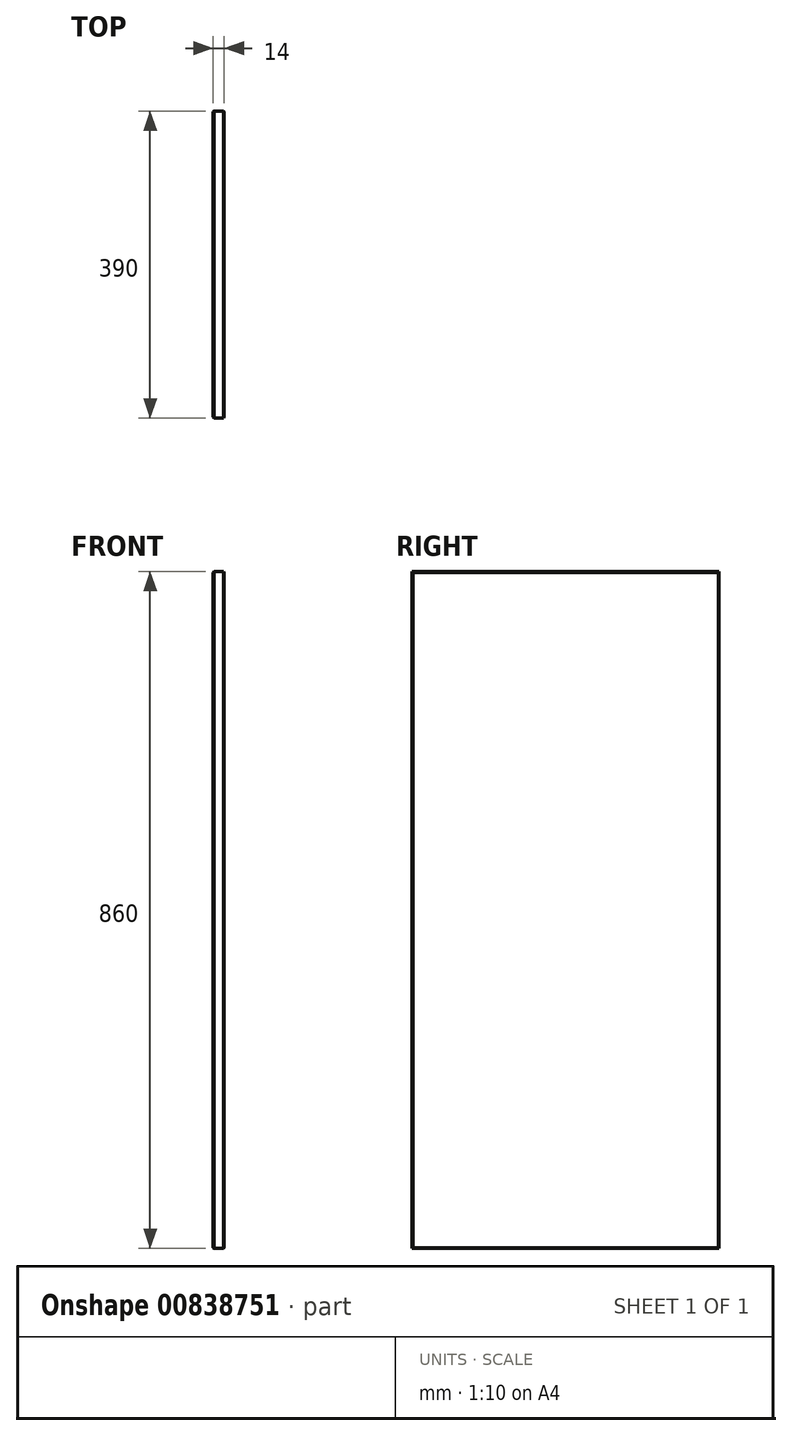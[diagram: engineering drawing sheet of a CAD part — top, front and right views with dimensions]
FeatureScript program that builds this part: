
annotation { "Feature Type Name" : "Feature", "Feature Type Description" : "" }
export const myFeature = defineFeature(function(context is Context, id is Id, definition is map)
    precondition{}
    {
        {
            var Q0;
            Q0=qCreatedBy(makeId("Right.planeOp"),FACE);
            var sketch = newSketch(context, id + "F0", { "sketchPlane" : qUnion([Q0])});
            skLineSegment(sketch, "E0.bottom", {"start": v(0, 0) * mm, "end": v(-55.42, 0) * mm});
            skLineSegment(sketch, "E0.top", {"start": v(0, 42.97) * mm, "end": v(-55.42, 42.97) * mm});
            skLineSegment(sketch, "E0.left", {"start": v(0, 0) * mm, "end": v(0, 42.97) * mm});
            skLineSegment(sketch, "E0.right", {"start": v(-55.42, 0) * mm, "end": v(-55.42, 42.97) * mm});
            skSolve(sketch);
        }
        {
            var Q0;
            Q0=makeQuery(id+"F0.imprint","IMPRINT",FACE,{"disambiguationData":[TD([[makeQuery(id+"F0.imprint","IMPRINT",EDGE,{"derivedFrom":sQuery(id+"F0.wireOp",EDGE,"E0.bottom")}),-1.0]])]});
            extrude(context, id + "F1", {"entities" : qUnion([Q0]), "oppositeDirection" : true, "depth" : 14 * mm, "offsetDistance" : 25 * mm});
        }
        {
            var Q0;
            Q0=makeQuery(id+"F1.opExtrude","SWEPT_FACE",FACE,{"disambiguationData":[OSD([sQuery(id+"F0.wireOp",EDGE,"E0.bottom")])]});
            extrude(context, id + "F2", {"entities" : qUnion([Q0]), "operationType" : NewBodyOperationType.ADD, "oppositeDirection" : true, "depth" : 1060 * mm, "offsetDistance" : 25 * mm});
        }
        {
            var Q0;
            {var subQ0=sQuery(id+"F0.wireOp",EDGE,"E0.left");Q0=makeQuery(id+"F2.boolean.opBoolean","MERGE",FACE,{"derivedFrom":[makeQuery(id+"F1.opExtrude","SWEPT_FACE",FACE,{"disambiguationData":[OSD([subQ0])]}),makeQuery(id+"F2.opExtrude","SWEPT_FACE",FACE,{"disambiguationData":[OSD([sQuery(id+"F0.wireOp",EDGE,"E0.bottom"),subQ0])]})]});}
            extrude(context, id + "F3", {"entities" : qUnion([Q0]), "operationType" : NewBodyOperationType.ADD, "oppositeDirection" : true, "depth" : 390 * mm, "offsetDistance" : 25 * mm});
        }
        {
            var Q0;
            {var subQ0=sQuery(id+"F0.wireOp",EDGE,"E0.left");var subQ1=sQuery(id+"F0.wireOp",EDGE,"E0.bottom");Q0=makeQuery(id+"F3.boolean.opBoolean","MERGE",FACE,{"derivedFrom":[makeQuery(id+"F2.opExtrude","CAP_FACE",FACE,{"disambiguationData":[OSD([subQ1])],"isStart":false}),makeQuery(id+"F3.opExtrude","SWEPT_FACE",FACE,{"disambiguationData":[OSD([subQ1,subQ0]),TDD([makeQuery(id+"F2.opExtrude","CAP_EDGE",EDGE,{"disambiguationData":[OSD([subQ1,subQ0])],"isStart":false})])]})]});}
            extrude(context, id + "F4", {"entities" : qUnion([Q0]), "operationType" : NewBodyOperationType.REMOVE, "oppositeDirection" : true, "depth" : 200 * mm, "offsetDistance" : 25 * mm});
        }
        {
            var Q0;
            {var subQ0=sQuery(id+"F0.wireOp",EDGE,"E0.left");var subQ1=sQuery(id+"F0.wireOp",EDGE,"E0.bottom");Q0=makeQuery(id+"F3.boolean.opBoolean","MERGE",FACE,{"derivedFrom":[makeQuery(id+"F2.boolean.opBoolean","MERGE",FACE,{"derivedFrom":[makeQuery(id+"F1.opExtrude","CAP_FACE",FACE,{"disambiguationData":[OSD([subQ1,sQuery(id+"F0.wireOp",EDGE,"E0.top"),subQ0,sQuery(id+"F0.wireOp",EDGE,"E0.right")])],"isStart":true}),makeQuery(id+"F2.opExtrude","SWEPT_FACE",FACE,{"disambiguationData":[OSD([subQ1]),TDD([makeQuery(id+"F1.opExtrude","CAP_EDGE",EDGE,{"disambiguationData":[OSD([subQ1])],"isStart":true})])]})]}),makeQuery(id+"F3.opExtrude","SWEPT_FACE",FACE,{"disambiguationData":[OSD([subQ1,subQ0]),TDD([makeQuery(id+"F2.boolean.opBoolean","MERGE",EDGE,{"derivedFrom":[makeQuery(id+"F1.opExtrude","CAP_EDGE",EDGE,{"disambiguationData":[OSD([subQ0])],"isStart":true}),makeQuery(id+"F2.opExtrude","SWEPT_EDGE",EDGE,{"disambiguationData":[OSD([subQ1,subQ0]),TDD([makeQuery(id+"F1.opExtrude","CAP_VERTEX",VERTEX,{"disambiguationData":[OSD([subQ1,subQ0])],"isStart":true})])]})]})])]})]});}
            var Q1;
            {var subQ0=sQuery(id+"F0.wireOp",EDGE,"E0.left");var subQ1=sQuery(id+"F0.wireOp",EDGE,"E0.bottom");Q1=makeQuery(id+"F3.boolean.opBoolean","MERGE",FACE,{"derivedFrom":[makeQuery(id+"F2.boolean.opBoolean","MERGE",FACE,{"derivedFrom":[makeQuery(id+"F1.opExtrude","CAP_FACE",FACE,{"disambiguationData":[OSD([subQ1,sQuery(id+"F0.wireOp",EDGE,"E0.top"),subQ0,sQuery(id+"F0.wireOp",EDGE,"E0.right")])],"isStart":false}),makeQuery(id+"F2.opExtrude","SWEPT_FACE",FACE,{"disambiguationData":[OSD([subQ1]),TDD([makeQuery(id+"F1.opExtrude","CAP_EDGE",EDGE,{"disambiguationData":[OSD([subQ1])],"isStart":false})])]})]}),makeQuery(id+"F3.opExtrude","SWEPT_FACE",FACE,{"disambiguationData":[OSD([subQ1,subQ0]),TDD([makeQuery(id+"F2.boolean.opBoolean","MERGE",EDGE,{"derivedFrom":[makeQuery(id+"F1.opExtrude","CAP_EDGE",EDGE,{"disambiguationData":[OSD([subQ0])],"isStart":false}),makeQuery(id+"F2.opExtrude","SWEPT_EDGE",EDGE,{"disambiguationData":[OSD([subQ1,subQ0]),TDD([makeQuery(id+"F1.opExtrude","CAP_VERTEX",VERTEX,{"disambiguationData":[OSD([subQ1,subQ0])],"isStart":false})])]})]})])]})]});}
            chamfer(context, id + "F5", {"entities" : qUnion([Q0, Q1]), "width" : 1 * mm, "tangentPropagation" : true});
        }
    });
